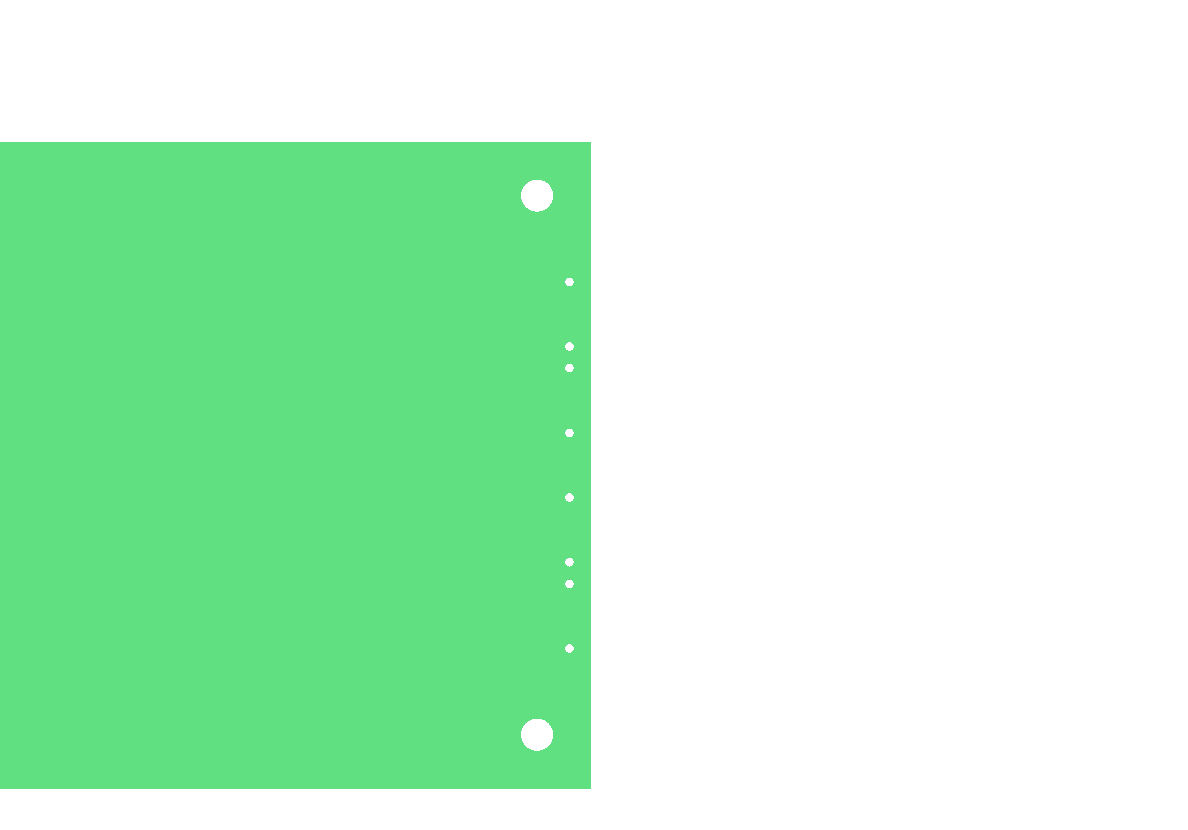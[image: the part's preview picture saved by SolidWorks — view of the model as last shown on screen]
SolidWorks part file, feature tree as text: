
SOLIDWORKS PART (.sldprt)
format: sldprt  version: not decoded by parser v0  size: 200,192 bytes
history: native  units: mm
features: sketch x4, cut_extrude x3, material x1, extrude x1, pattern_linear x1 (+13 scaffold rows collapsed)
feature tree (23):
  scaffold x13  (default folders/planes/origin — collapsed)
  material  "Material <not specified>"
  sketch  "Sketch1"  dims[D1=158.75mm D2=76.2mm]
  extrude  "Extrude1"  Depth=1.5748mm
  sketch  "Sketch2"  dims[c1.D1=~1.999298mm c1.D5=3.81mm c1.D6=3.81mm c1.D11=3.81mm c1.D12=3.81mm c2.D1=6.35mm c2.D2=6.35mm c2.D3=6.35mm c2.D4=6.35mm c2.D7=6.35mm c2.D8=6.35mm c2.D9=6.35mm c2.D10=6.35mm]
  cut_extrude  "Cut-Extrude2"  Depth=1.5748mm
  sketch  "Sketch4"  dims[c1.D1=1.3mm c1.D2=1.3mm c1.D10=1.0mm c1.D11=1.0mm c1.D3=~19.234912mm c1.D4=7.55mm c1.D5=~19.234912mm c1.D6=7.55mm c1.D7=~37.730176mm c1.D8=43.53mm c1.D9=5.95mm c1.D12=~36.528293mm c1.D13=~39.671707mm c2.D12=~16.334994mm c2.D13=~16.335006mm]
  cut_extrude  "Cut-Extrude3"  Depth=1.5748mm
  sketch  "Sketch5"  dims[D1=1.016mm D7=1.016mm D8=1.016mm D9=1.016mm D2=16.51mm D3=2.54mm D4=7.62mm D5=2.54mm D6=7.62mm]
  cut_extrude  "transceiver holes"  Depth=2.54mm
  pattern_linear  "LPattern1"  Count1=2 Count2=1 Spacing1=25.4mm Spacing2=7.62mm
decode coverage: 9 of 9 modeling features carry decoded parameters
note: ~ marks probable driven/reference dimensions
note: suppression state not decoded; provenance and decode notes live in map.json
